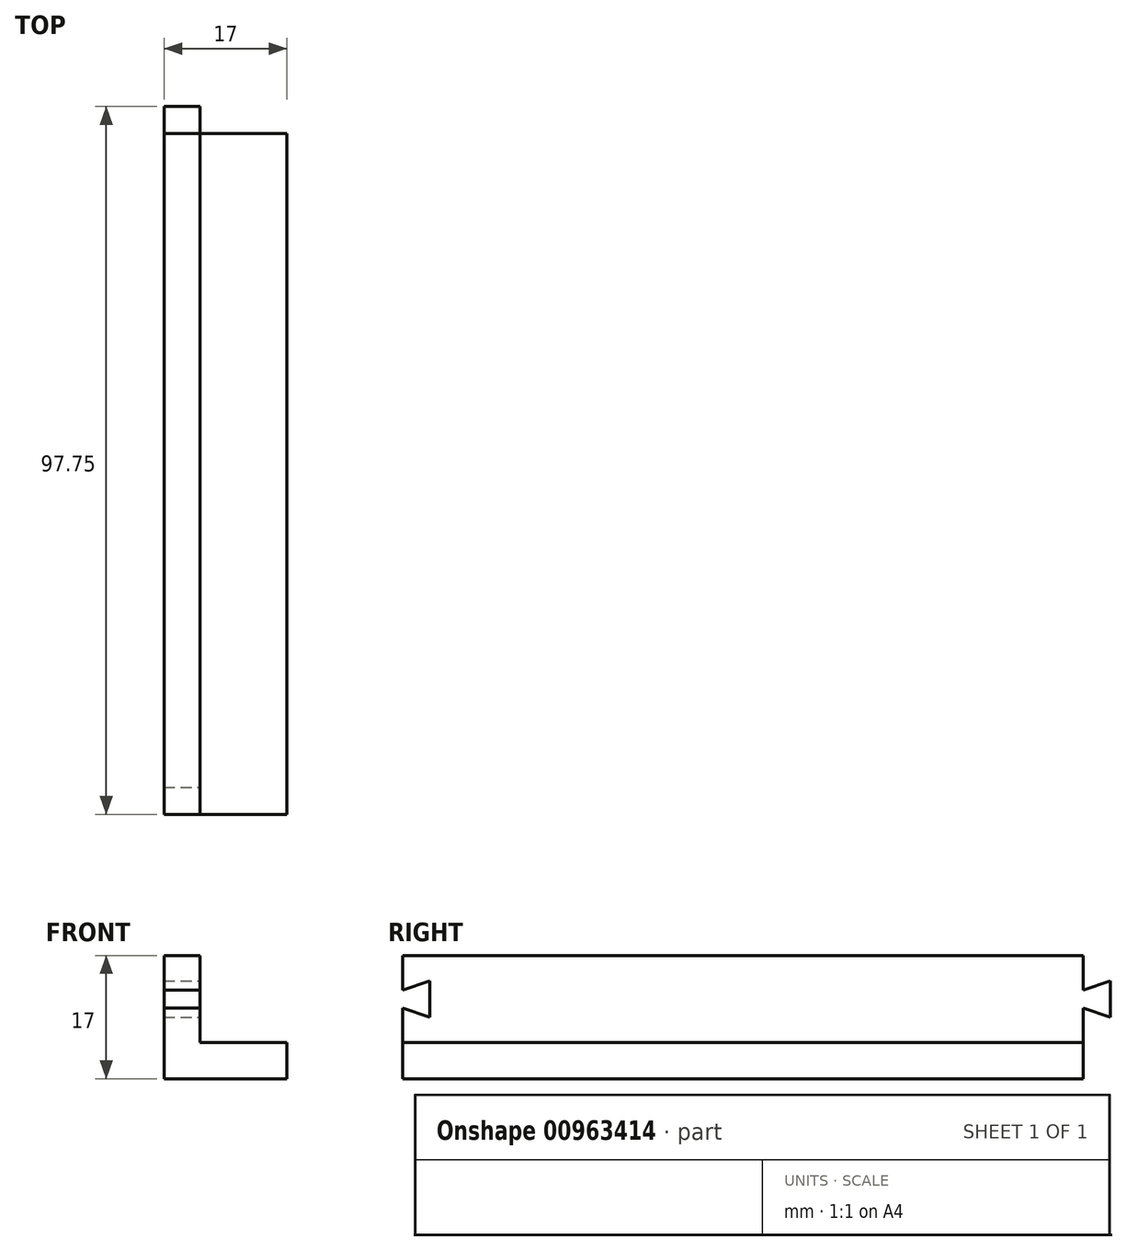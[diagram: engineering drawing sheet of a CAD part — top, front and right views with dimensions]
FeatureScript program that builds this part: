
annotation { "Feature Type Name" : "Feature", "Feature Type Description" : "" }
export const myFeature = defineFeature(function(context is Context, id is Id, definition is map)
    precondition{}
    {
        {
            var Q0;
            Q0=qCreatedBy(makeId("Top.planeOp"),FACE);
            var sketch = newSketch(context, id + "F0", { "sketchPlane" : qUnion([Q0])});
            skLineSegment(sketch, "E0.bottom", {"start": v(8.5, -47) * mm, "end": v(-8.5, -47) * mm});
            skLineSegment(sketch, "E0.top", {"start": v(8.5, 47) * mm, "end": v(-8.5, 47) * mm});
            skLineSegment(sketch, "E0.left", {"start": v(8.5, -47) * mm, "end": v(8.5, 47) * mm});
            skLineSegment(sketch, "E0.right", {"start": v(-8.5, -47) * mm, "end": v(-8.5, 47) * mm});
            skPoint(sketch, "E0.middle", {"position": v(0, 0) * mm});
            skLineSegment(sketch, "E1", {"start": v(3.75, 47) * mm, "end": v(1.25, 47) * mm});
            skSolve(sketch);
        }
        {
            var Q0;
            Q0=makeQuery(id+"F0.imprint","IMPRINT",FACE,{"disambiguationData":[TD([[makeQuery(id+"F0.imprint","IMPRINT",EDGE,{"derivedFrom":sQuery(id+"F0.wireOp",EDGE,"E0.bottom")}),-1.0]])]});
            extrude(context, id + "F1", {"entities" : qUnion([Q0]), "depth" : 5 * mm, "offsetDistance" : 25 * mm});
        }
        {
            var Q0;
            Q0=makeQuery(id+"F1.opExtrude","CAP_FACE",FACE,{"disambiguationData":[OSD([sQuery(id+"F0.wireOp",EDGE,"E0.bottom"),sQuery(id+"F0.wireOp",EDGE,"E0.top"),sQuery(id+"F0.wireOp",EDGE,"E0.left"),sQuery(id+"F0.wireOp",EDGE,"E0.right"),sQuery(id+"F0.wireOp",EDGE,"rw5FdkIU-7Pyv-DcX8-fDZG-QsmjpqUQaUpg"),sQuery(id+"F0.wireOp",EDGE,"jVwzFZEz-LamF-PFxA-NCYc-S7eYUaHMYtTf"),sQuery(id+"F0.wireOp",EDGE,"HgkX7Yv0-hTDJ-ucJP-wwuC-oNEPRnFH2NnW"),sQuery(id+"F0.wireOp",EDGE,"0Pd2xpSO-AvzK-sIeG-jRaa-LW2rH33TRvBc")])],"isStart":false});
            var sketch = newSketch(context, id + "F2", { "sketchPlane" : qUnion([Q0])});
            skLineSegment(sketch, "E2.bottom", {"start": v(-8.5, 47) * mm, "end": v(-3.5, 47) * mm});
            skLineSegment(sketch, "E2.top", {"start": v(-8.5, -47) * mm, "end": v(-3.5, -47) * mm});
            skLineSegment(sketch, "E2.left", {"start": v(-8.5, 47) * mm, "end": v(-8.5, -47) * mm});
            skLineSegment(sketch, "E2.right", {"start": v(-3.5, 47) * mm, "end": v(-3.5, -47) * mm});
            skSolve(sketch);
        }
        {
            var Q0;
            Q0=makeQuery(id+"F2.imprint","IMPRINT",FACE,{"disambiguationData":[TD([[makeQuery(id+"F2.imprint","IMPRINT",EDGE,{"derivedFrom":sQuery(id+"F2.wireOp",EDGE,"E2.bottom")}),1.0]])]});
            extrude(context, id + "F3", {"entities" : qUnion([Q0]), "operationType" : NewBodyOperationType.ADD, "depth" : 12 * mm, "offsetDistance" : 25 * mm});
        }
        {
            var Q0;
            Q0=makeQuery(id+"F3.opExtrude","SWEPT_FACE",FACE,{"disambiguationData":[OSD([sQuery(id+"F2.wireOp",EDGE,"E2.right")])]});
            var sketch = newSketch(context, id + "F4", { "sketchPlane" : qUnion([Q0])});
            skLineSegment(sketch, "E3", {"start": v(47, 17) * mm, "end": v(47, 5) * mm, "construction": true});
            skPoint(sketch, "E4", {"position": v(47, 12.25) * mm});
            skPoint(sketch, "E5", {"position": v(47, 9.75) * mm});
            skPoint(sketch, "E6", {"position": v(47, 13.5) * mm});
            skPoint(sketch, "E7", {"position": v(47, 8.5) * mm});
            skLineSegment(sketch, "E8.MirrorCS", {"start": v(47, 12.25) * mm, "end": v(50.75, 13.5) * mm});
            skLineSegment(sketch, "E9.MirrorCS", {"start": v(50.75, 8.5) * mm, "end": v(47, 9.75) * mm});
            skLineSegment(sketch, "E10", {"start": v(47, 12.25) * mm, "end": v(47, 9.75) * mm});
            skLineSegment(sketch, "E11", {"start": v(47, 13.5) * mm, "end": v(50.75, 13.5) * mm, "construction": true});
            skLineSegment(sketch, "E12", {"start": v(50.75, 8.5) * mm, "end": v(47, 8.5) * mm, "construction": true});
            skLineSegment(sketch, "E13", {"start": v(50.75, 13.5) * mm, "end": v(50.75, 8.5) * mm});
            skSolve(sketch);
        }
        {
            var Q0;
            Q0=makeQuery(id+"F4.imprint","IMPRINT",FACE,{"disambiguationData":[TD([[makeQuery(id+"F4.imprint","IMPRINT",EDGE,{"derivedFrom":sQuery(id+"F4.wireOp",EDGE,"E8.MirrorCS")}),-1.0]])]});
            extrude(context, id + "F5", {"entities" : qUnion([Q0]), "oppositeDirection" : true, "depth" : 5 * mm, "offsetDistance" : 25 * mm});
        }
        {
            var Q0;
            Q0=makeQuery(id+"F1.opExtrude","SWEPT_BODY",BODY,{"disambiguationData":[OSD([sQuery(id+"F0.wireOp",EDGE,"E0.bottom"),sQuery(id+"F0.wireOp",EDGE,"E0.top"),sQuery(id+"F0.wireOp",EDGE,"E0.left"),sQuery(id+"F0.wireOp",EDGE,"E0.right"),sQuery(id+"F0.wireOp",EDGE,"rw5FdkIU-7Pyv-DcX8-fDZG-QsmjpqUQaUpg"),sQuery(id+"F0.wireOp",EDGE,"0Pd2xpSO-AvzK-sIeG-jRaa-LW2rH33TRvBc"),sQuery(id+"F0.wireOp",EDGE,"I78ihydD-mLBZ-YjAQ-QUO5-5Q7WJKXBQuCR")])]});
            var Q1;
            Q1=makeQuery(id+"F5.opExtrude","SWEPT_BODY",BODY,{"disambiguationData":[OSD([sQuery(id+"F4.wireOp",EDGE,"E8.MirrorCS"),sQuery(id+"F4.wireOp",EDGE,"E9.MirrorCS"),sQuery(id+"F4.wireOp",EDGE,"E10"),sQuery(id+"F4.wireOp",EDGE,"E13")])]});
            booleanBodies(context, id + "F6", {"operationType" : BooleanOperationType.UNION, "tools" : qUnion([Q0, Q1])});
        }
        {
            var Q0;
            Q0=makeQuery(id+"F6.opBoolean","MERGE",FACE,{"derivedFrom":[makeQuery(id+"F3.opExtrude","SWEPT_FACE",FACE,{"disambiguationData":[OSD([sQuery(id+"F2.wireOp",EDGE,"E2.right")])]}),makeQuery(id+"F5.opExtrude","CAP_FACE",FACE,{"disambiguationData":[OSD([sQuery(id+"F4.wireOp",EDGE,"E8.MirrorCS"),sQuery(id+"F4.wireOp",EDGE,"E9.MirrorCS"),sQuery(id+"F4.wireOp",EDGE,"E10"),sQuery(id+"F4.wireOp",EDGE,"E13")])],"isStart":true})]});
            var sketch = newSketch(context, id + "F7", { "sketchPlane" : qUnion([Q0])});
            skLineSegment(sketch, "E14", {"start": v(-47, 5) * mm, "end": v(-47, 17) * mm, "construction": true});
            skPoint(sketch, "E15", {"position": v(-47, 8.5) * mm});
            skPoint(sketch, "E16", {"position": v(-47, 12.25) * mm});
            skPoint(sketch, "E17", {"position": v(-47, 13.5) * mm});
            skPoint(sketch, "E18", {"position": v(-47, 9.75) * mm});
            skLineSegment(sketch, "E19", {"start": v(-47, 9.75) * mm, "end": v(-43.25, 8.5) * mm});
            skLineSegment(sketch, "E20", {"start": v(-43.25, 8.5) * mm, "end": v(-43.25, 13.5) * mm});
            skLineSegment(sketch, "E21", {"start": v(-43.25, 13.5) * mm, "end": v(-47, 12.25) * mm});
            skLineSegment(sketch, "E22", {"start": v(-47, 9.75) * mm, "end": v(-47, 12.25) * mm});
            skSolve(sketch);
        }
        {
            var Q0;
            Q0=makeQuery(id+"F7.imprint","IMPRINT",FACE,{"disambiguationData":[TD([[makeQuery(id+"F7.imprint","IMPRINT",EDGE,{"derivedFrom":sQuery(id+"F7.wireOp",EDGE,"E19")}),1.0]])]});
            extrude(context, id + "F8", {"entities" : qUnion([Q0]), "operationType" : NewBodyOperationType.REMOVE, "oppositeDirection" : true, "depth" : 5 * mm, "offsetDistance" : 25 * mm});
        }
    });
